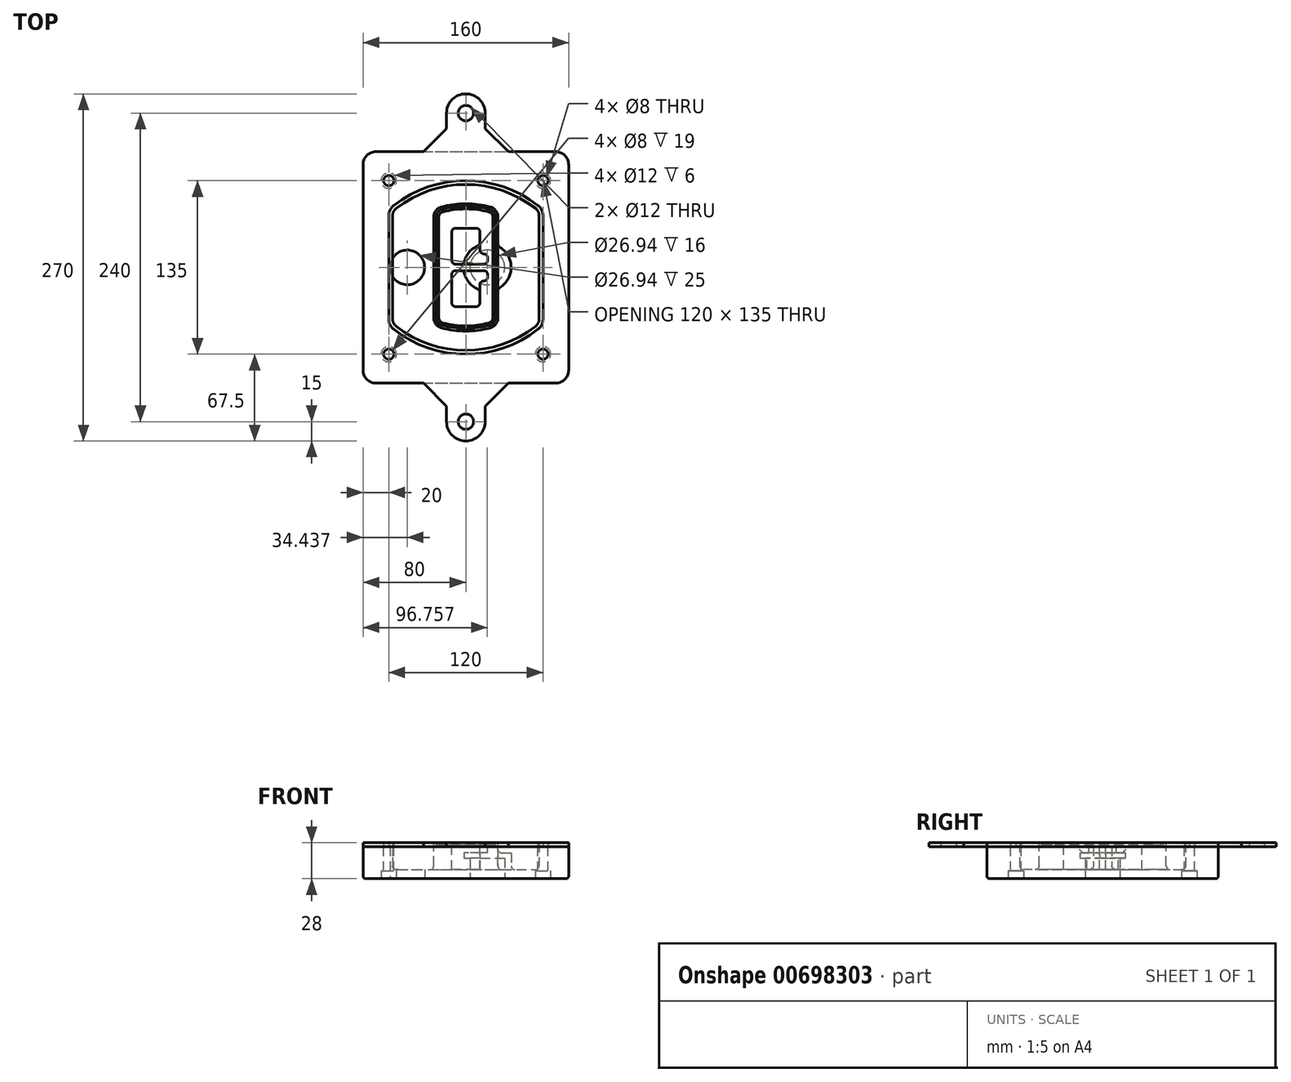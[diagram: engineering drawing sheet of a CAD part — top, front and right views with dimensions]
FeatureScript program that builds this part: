
annotation { "Feature Type Name" : "Feature", "Feature Type Description" : "" }
export const myFeature = defineFeature(function(context is Context, id is Id, definition is map)
    precondition{}
    {
        {
            var Q0;
            Q0=qCreatedBy(makeId("Top.planeOp"),FACE);
            var sketch = newSketch(context, id + "F0", { "sketchPlane" : qUnion([Q0])});
            skPoint(sketch, "E0.rect.middle", {"position": v(0, 0) * mm});
            skLineSegment(sketch, "E1.bottom", {"start": v(-70, -90) * mm, "end": v(70, -90) * mm});
            skLineSegment(sketch, "E1.top", {"start": v(-70, 90) * mm, "end": v(70, 90) * mm});
            skLineSegment(sketch, "E1.left", {"start": v(-80, -80) * mm, "end": v(-80, 80) * mm});
            skLineSegment(sketch, "E1.right", {"start": v(80, -80) * mm, "end": v(80, 80) * mm});
            skLineSegment(sketch, "E2", {"start": v(-80, 90) * mm, "end": v(80, -90) * mm, "construction": true});
            skLineSegment(sketch, "E3", {"start": v(80, 90) * mm, "end": v(-80, -90) * mm, "construction": true});
            skCircle(sketch, "E4", {"center": v(-60, 67.5) * mm, "radius": 4 * mm});
            skCircle(sketch, "E5", {"center": v(60, 67.5) * mm, "radius": 4 * mm});
            skCircle(sketch, "E6", {"center": v(60, -67.5) * mm, "radius": 4 * mm});
            skCircle(sketch, "E7", {"center": v(-60, -67.5) * mm, "radius": 4 * mm});
            skLineSegment(sketch, "E8", {"start": v(-60, 67.5) * mm, "end": v(60, 67.5) * mm, "construction": true});
            skLineSegment(sketch, "E9", {"start": v(60, 67.5) * mm, "end": v(60, -67.5) * mm, "construction": true});
            skLineSegment(sketch, "E10", {"start": v(60, -67.5) * mm, "end": v(-60, -67.5) * mm, "construction": true});
            skLineSegment(sketch, "E11", {"start": v(-60, -67.5) * mm, "end": v(-60, 67.5) * mm, "construction": true});
            skLineSegment(sketch, "E12", {"start": v(-60, 40.3) * mm, "end": v(-60, -40.3) * mm});
            skLineSegment(sketch, "E13", {"start": v(60, 40.3) * mm, "end": v(60, -40.3) * mm});
            skArc(sketch, "E14", {"start": v(56.15, 48.18) * mm, "mid": v(0, 67.5) * mm, "end": v(-56.15, 48.18) * mm});
            skArc(sketch, "E15", {"start": v(-56.15, -48.18) * mm, "mid": v(0, -67.5) * mm, "end": v(56.15, -48.18) * mm});
            skLineSegment(sketch, "E16", {"start": v(-60, 0) * mm, "end": v(60, 0) * mm, "construction": true});
            skPoint(sketch, "E17.visualSharp", {"position": v(-60, -45) * mm});
            skArc(sketch, "E17.filletArc", {"start": v(-60, -40.3) * mm, "mid": v(-58.99, -44.68) * mm, "end": v(-56.15, -48.18) * mm});
            skPoint(sketch, "E18.visualSharp", {"position": v(-60, 45) * mm});
            skArc(sketch, "E18.filletArc", {"start": v(-56.15, 48.18) * mm, "mid": v(-58.99, 44.68) * mm, "end": v(-60, 40.3) * mm});
            skPoint(sketch, "E19.visualSharp", {"position": v(60, 45) * mm});
            skArc(sketch, "E19.filletArc", {"start": v(60, 40.3) * mm, "mid": v(58.99, 44.68) * mm, "end": v(56.15, 48.18) * mm});
            skPoint(sketch, "E20.visualSharp", {"position": v(60, -45) * mm});
            skArc(sketch, "E20.filletArc", {"start": v(56.15, -48.18) * mm, "mid": v(58.99, -44.68) * mm, "end": v(60, -40.3) * mm});
            skPoint(sketch, "E21.visualSharp", {"position": v(-80, 90) * mm});
            skArc(sketch, "E21.filletArc", {"start": v(-70, 90) * mm, "mid": v(-77.07, 87.07) * mm, "end": v(-80, 80) * mm});
            skPoint(sketch, "E22.visualSharp", {"position": v(80, 90) * mm});
            skArc(sketch, "E22.filletArc", {"start": v(80, 80) * mm, "mid": v(77.07, 87.07) * mm, "end": v(70, 90) * mm});
            skPoint(sketch, "E23.visualSharp", {"position": v(80, -90) * mm});
            skArc(sketch, "E23.filletArc", {"start": v(70, -90) * mm, "mid": v(77.07, -87.07) * mm, "end": v(80, -80) * mm});
            skPoint(sketch, "E24.visualSharp", {"position": v(-80, -90) * mm});
            skArc(sketch, "E24.filletArc", {"start": v(-80, -80) * mm, "mid": v(-77.07, -87.07) * mm, "end": v(-70, -90) * mm});
            skArc(sketch, "E25.0", {"start": v(57, 40.3) * mm, "mid": v(56.3, 43.36) * mm, "end": v(54.3, 45.81) * mm});
            skLineSegment(sketch, "E25.1", {"start": v(57, 40.3) * mm, "end": v(57, -40.3) * mm});
            skArc(sketch, "E25.2", {"start": v(54.3, -45.81) * mm, "mid": v(56.3, -43.36) * mm, "end": v(57, -40.3) * mm});
            skArc(sketch, "E25.3", {"start": v(-54.3, -45.81) * mm, "mid": v(0, -64.5) * mm, "end": v(54.3, -45.81) * mm});
            skArc(sketch, "E25.4", {"start": v(-57, -40.3) * mm, "mid": v(-56.3, -43.36) * mm, "end": v(-54.3, -45.81) * mm});
            skArc(sketch, "E25.5", {"start": v(54.3, 45.81) * mm, "mid": v(0, 64.5) * mm, "end": v(-54.3, 45.81) * mm});
            skLineSegment(sketch, "E25.6", {"start": v(-57, 40.3) * mm, "end": v(-57, -40.3) * mm});
            skArc(sketch, "E25.7", {"start": v(-54.3, 45.81) * mm, "mid": v(-56.3, 43.36) * mm, "end": v(-57, 40.3) * mm});
            skArc(sketch, "E26.0", {"start": v(-58.62, 51.33) * mm, "mid": v(-62.58, 46.43) * mm, "end": v(-64, 40.3) * mm});
            skArc(sketch, "E26.1", {"start": v(58.62, 51.33) * mm, "mid": v(0, 71.5) * mm, "end": v(-58.62, 51.33) * mm});
            skArc(sketch, "E26.2", {"start": v(64, 40.3) * mm, "mid": v(62.58, 46.43) * mm, "end": v(58.62, 51.33) * mm});
            skLineSegment(sketch, "E26.3", {"start": v(64, 40.3) * mm, "end": v(64, -40.3) * mm});
            skArc(sketch, "E26.4", {"start": v(58.62, -51.33) * mm, "mid": v(62.58, -46.43) * mm, "end": v(64, -40.3) * mm});
            skLineSegment(sketch, "E26.5", {"start": v(-64, 40.3) * mm, "end": v(-64, -40.3) * mm});
            skArc(sketch, "E26.6", {"start": v(-58.62, -51.33) * mm, "mid": v(0, -71.5) * mm, "end": v(58.62, -51.33) * mm});
            skArc(sketch, "E26.7", {"start": v(-64, -40.3) * mm, "mid": v(-62.58, -46.43) * mm, "end": v(-58.62, -51.33) * mm});
            skSolve(sketch);
        }
        {
            var Q0;
            Q0=makeQuery(id+"F0.imprint","IMPRINT",FACE,{"disambiguationData":[TD([[makeQuery(id+"F0.imprint","IMPRINT",EDGE,{"derivedFrom":sQuery(id+"F0.wireOp",EDGE,"E1.bottom")}),1.0]])]});
            var Q1;
            Q1=makeQuery(id+"F0.imprint","IMPRINT",FACE,{"disambiguationData":[TD([[makeQuery(id+"F0.imprint","IMPRINT",EDGE,{"derivedFrom":sQuery(id+"F0.wireOp",EDGE,"E12")}),1.0]])]});
            var Q2;
            Q2=makeQuery(id+"F0.imprint","IMPRINT",FACE,{"disambiguationData":[TD([[makeQuery(id+"F0.imprint","IMPRINT",EDGE,{"derivedFrom":sQuery(id+"F0.wireOp",EDGE,"E25.0")}),1.0]])]});
            var Q3;
            Q3=makeQuery(id+"F0.imprint","IMPRINT",FACE,{"disambiguationData":[TD([[makeQuery(id+"F0.imprint","IMPRINT",EDGE,{"derivedFrom":sQuery(id+"F0.wireOp",EDGE,"E12")}),-1.0]])]});
            extrude(context, id + "F1", {"entities" : qUnion([Q0, Q1, Q2, Q3]), "oppositeDirection" : true, "depth" : 25 * mm, "offsetDistance" : 25 * mm});
        }
        {
            var Q0;
            Q0=makeQuery(id+"F0.imprint","IMPRINT",FACE,{"disambiguationData":[TD([[makeQuery(id+"F0.imprint","IMPRINT",EDGE,{"derivedFrom":sQuery(id+"F0.wireOp",EDGE,"E12")}),1.0]])]});
            extrude(context, id + "F2", {"entities" : qUnion([Q0]), "operationType" : NewBodyOperationType.ADD, "depth" : 3 * mm, "offsetDistance" : 25 * mm});
        }
        {
            var Q0;
            Q0=makeQuery(id+"F0.imprint","IMPRINT",FACE,{"disambiguationData":[TD([[makeQuery(id+"F0.imprint","IMPRINT",EDGE,{"derivedFrom":sQuery(id+"F0.wireOp",EDGE,"E25.0")}),1.0]])]});
            extrude(context, id + "F3", {"entities" : qUnion([Q0]), "operationType" : NewBodyOperationType.REMOVE, "oppositeDirection" : true, "depth" : 18 * mm});
        }
        {
            var Q0;
            Q0=makeQuery(id+"F2.opExtrude","CAP_FACE",FACE,{"disambiguationData":[OSD([sQuery(id+"F0.wireOp",EDGE,"E12"),sQuery(id+"F0.wireOp",EDGE,"E13"),sQuery(id+"F0.wireOp",EDGE,"E14"),sQuery(id+"F0.wireOp",EDGE,"E15"),sQuery(id+"F0.wireOp",EDGE,"E17.filletArc"),sQuery(id+"F0.wireOp",EDGE,"E18.filletArc"),sQuery(id+"F0.wireOp",EDGE,"E19.filletArc"),sQuery(id+"F0.wireOp",EDGE,"E20.filletArc"),sQuery(id+"F0.wireOp",EDGE,"E25.0"),sQuery(id+"F0.wireOp",EDGE,"E25.1"),sQuery(id+"F0.wireOp",EDGE,"E25.2"),sQuery(id+"F0.wireOp",EDGE,"E25.3"),sQuery(id+"F0.wireOp",EDGE,"E25.4"),sQuery(id+"F0.wireOp",EDGE,"E25.5"),sQuery(id+"F0.wireOp",EDGE,"E25.6"),sQuery(id+"F0.wireOp",EDGE,"E25.7")])],"isStart":false});
            var sketch = newSketch(context, id + "F4", { "sketchPlane" : qUnion([Q0])});
            skArc(sketch, "E27.0", {"start": v(-19.08, -46.97) * mm, "mid": v(0, -49.5) * mm, "end": v(19.08, -46.97) * mm});
            skArc(sketch, "E28.0", {"start": v(19.08, 46.97) * mm, "mid": v(0, 49.5) * mm, "end": v(-19.08, 46.97) * mm});
            skLineSegment(sketch, "E29", {"start": v(-25, 39.25) * mm, "end": v(-25, -39.25) * mm});
            skLineSegment(sketch, "E30", {"start": v(25, 39.25) * mm, "end": v(25, -39.25) * mm});
            skLineSegment(sketch, "E31", {"start": v(-25, 45.1) * mm, "end": v(25, 45.1) * mm, "construction": true});
            skLineSegment(sketch, "E32", {"start": v(-25, -45.1) * mm, "end": v(25, -45.1) * mm, "construction": true});
            skPoint(sketch, "E33.visualSharp", {"position": v(-25, 45.1) * mm});
            skArc(sketch, "E33.filletArc", {"start": v(-19.08, 46.97) * mm, "mid": v(-23.35, 44.11) * mm, "end": v(-25, 39.25) * mm});
            skPoint(sketch, "E34.visualSharp", {"position": v(25, 45.1) * mm});
            skArc(sketch, "E34.filletArc", {"start": v(25, 39.25) * mm, "mid": v(23.35, 44.11) * mm, "end": v(19.08, 46.97) * mm});
            skPoint(sketch, "E35.visualSharp", {"position": v(25, -45.1) * mm});
            skArc(sketch, "E35.filletArc", {"start": v(19.08, -46.97) * mm, "mid": v(23.35, -44.11) * mm, "end": v(25, -39.25) * mm});
            skPoint(sketch, "E36.visualSharp", {"position": v(-25, -45.1) * mm});
            skArc(sketch, "E36.filletArc", {"start": v(-25, -39.25) * mm, "mid": v(-23.35, -44.11) * mm, "end": v(-19.08, -46.97) * mm});
            skArc(sketch, "E37.0", {"start": v(54.3, 45.81) * mm, "mid": v(0, 64.5) * mm, "end": v(-54.3, 45.81) * mm});
            skArc(sketch, "E37.1", {"start": v(-54.3, 45.81) * mm, "mid": v(-56.3, 43.36) * mm, "end": v(-57, 40.3) * mm});
            skLineSegment(sketch, "E37.2", {"start": v(-57, 40.3) * mm, "end": v(-57, -40.3) * mm});
            skArc(sketch, "E37.3", {"start": v(-57, -40.3) * mm, "mid": v(-56.3, -43.36) * mm, "end": v(-54.3, -45.81) * mm});
            skArc(sketch, "E37.4", {"start": v(-54.3, -45.81) * mm, "mid": v(0, -64.5) * mm, "end": v(54.3, -45.81) * mm});
            skArc(sketch, "E37.5", {"start": v(54.3, -45.81) * mm, "mid": v(56.3, -43.36) * mm, "end": v(57, -40.3) * mm});
            skLineSegment(sketch, "E37.6", {"start": v(57, 40.3) * mm, "end": v(57, -40.3) * mm});
            skArc(sketch, "E37.7", {"start": v(57, 40.3) * mm, "mid": v(56.3, 43.36) * mm, "end": v(54.3, 45.81) * mm});
            skLineSegment(sketch, "E38.0", {"start": v(23, 39.25) * mm, "end": v(23, -39.25) * mm});
            skArc(sketch, "E38.1", {"start": v(18.56, -45.04) * mm, "mid": v(21.76, -42.9) * mm, "end": v(23, -39.25) * mm});
            skArc(sketch, "E38.2", {"start": v(-18.56, -45.04) * mm, "mid": v(0, -47.5) * mm, "end": v(18.56, -45.04) * mm});
            skArc(sketch, "E38.3", {"start": v(-23, -39.25) * mm, "mid": v(-21.76, -42.9) * mm, "end": v(-18.56, -45.04) * mm});
            skLineSegment(sketch, "E38.4", {"start": v(-23, 39.25) * mm, "end": v(-23, -39.25) * mm});
            skArc(sketch, "E38.5", {"start": v(23, 39.25) * mm, "mid": v(21.76, 42.9) * mm, "end": v(18.56, 45.04) * mm});
            skArc(sketch, "E38.6", {"start": v(-18.56, 45.04) * mm, "mid": v(-21.76, 42.9) * mm, "end": v(-23, 39.25) * mm});
            skArc(sketch, "E38.7", {"start": v(18.56, 45.04) * mm, "mid": v(0, 47.5) * mm, "end": v(-18.56, 45.04) * mm});
            skArc(sketch, "E39.0", {"start": v(21, 39.25) * mm, "mid": v(20.18, 41.68) * mm, "end": v(18.04, 43.1) * mm});
            skLineSegment(sketch, "E39.1", {"start": v(21, 39.25) * mm, "end": v(21, -39.25) * mm});
            skArc(sketch, "E39.2", {"start": v(18.04, -43.1) * mm, "mid": v(20.18, -41.68) * mm, "end": v(21, -39.25) * mm});
            skArc(sketch, "E39.3", {"start": v(-18.04, -43.1) * mm, "mid": v(0, -45.5) * mm, "end": v(18.04, -43.1) * mm});
            skArc(sketch, "E39.4", {"start": v(-21, -39.25) * mm, "mid": v(-20.18, -41.68) * mm, "end": v(-18.04, -43.1) * mm});
            skArc(sketch, "E39.5", {"start": v(18.04, 43.1) * mm, "mid": v(0, 45.5) * mm, "end": v(-18.04, 43.1) * mm});
            skLineSegment(sketch, "E39.6", {"start": v(-21, 39.25) * mm, "end": v(-21, -39.25) * mm});
            skArc(sketch, "E39.7", {"start": v(-18.04, 43.1) * mm, "mid": v(-20.18, 41.68) * mm, "end": v(-21, 39.25) * mm});
            skLineSegment(sketch, "E40", {"start": v(-25, 0) * mm, "end": v(25, 0) * mm, "construction": true});
            skLineSegment(sketch, "E41", {"start": v(-11, 5.5) * mm, "end": v(-11, 27.5) * mm});
            skLineSegment(sketch, "E42", {"start": v(-8, 30.5) * mm, "end": v(8, 30.5) * mm});
            skLineSegment(sketch, "E43", {"start": v(11, 27.5) * mm, "end": v(11, 13.5) * mm});
            skLineSegment(sketch, "E44", {"start": v(14, 10.5) * mm, "end": v(14, 10.5) * mm});
            skLineSegment(sketch, "E45", {"start": v(17, 7.5) * mm, "end": v(17, 5.5) * mm});
            skLineSegment(sketch, "E46", {"start": v(14, 2.5) * mm, "end": v(-8, 2.5) * mm});
            skPoint(sketch, "E47.visualSharp", {"position": v(-11, 30.5) * mm});
            skArc(sketch, "E47.filletArc", {"start": v(-8, 30.5) * mm, "mid": v(-10.12, 29.62) * mm, "end": v(-11, 27.5) * mm});
            skPoint(sketch, "E48.visualSharp", {"position": v(11, 30.5) * mm});
            skArc(sketch, "E48.filletArc", {"start": v(11, 27.5) * mm, "mid": v(10.12, 29.62) * mm, "end": v(8, 30.5) * mm});
            skPoint(sketch, "E49.visualSharp", {"position": v(11, 10.5) * mm});
            skArc(sketch, "E49.filletArc", {"start": v(11, 13.5) * mm, "mid": v(11.88, 11.38) * mm, "end": v(14, 10.5) * mm});
            skPoint(sketch, "E50.visualSharp", {"position": v(17, 10.5) * mm});
            skArc(sketch, "E50.filletArc", {"start": v(17, 7.5) * mm, "mid": v(16.12, 9.62) * mm, "end": v(14, 10.5) * mm});
            skPoint(sketch, "E51.visualSharp", {"position": v(17, 2.5) * mm});
            skArc(sketch, "E51.filletArc", {"start": v(14, 2.5) * mm, "mid": v(16.12, 3.38) * mm, "end": v(17, 5.5) * mm});
            skPoint(sketch, "E52.visualSharp", {"position": v(-11, 2.5) * mm});
            skArc(sketch, "E52.filletArc", {"start": v(-11, 5.5) * mm, "mid": v(-10.12, 3.38) * mm, "end": v(-8, 2.5) * mm});
            skLineSegment(sketch, "E53.0.MirrorCS", {"start": v(14, -2.5) * mm, "end": v(-8, -2.5) * mm});
            skArc(sketch, "E54.0.MirrorCS", {"start": v(-11, -5.5) * mm, "mid": v(-10.12, -3.38) * mm, "end": v(-8, -2.5) * mm});
            skLineSegment(sketch, "E55.0.MirrorCS", {"start": v(-11, -5.5) * mm, "end": v(-11, -27.5) * mm});
            skArc(sketch, "E56.0.MirrorCS", {"start": v(-8, -30.5) * mm, "mid": v(-10.12, -29.62) * mm, "end": v(-11, -27.5) * mm});
            skLineSegment(sketch, "E57.0.MirrorCS", {"start": v(-8, -30.5) * mm, "end": v(8, -30.5) * mm});
            skArc(sketch, "E58.0.MirrorCS", {"start": v(11, -27.5) * mm, "mid": v(10.12, -29.62) * mm, "end": v(8, -30.5) * mm});
            skLineSegment(sketch, "E59.0.MirrorCS", {"start": v(11, -27.5) * mm, "end": v(11, -13.5) * mm});
            skArc(sketch, "E60.0.MirrorCS", {"start": v(11, -13.5) * mm, "mid": v(11.88, -11.38) * mm, "end": v(14, -10.5) * mm});
            skArc(sketch, "E61.0.MirrorCS", {"start": v(17, -7.5) * mm, "mid": v(16.12, -9.62) * mm, "end": v(14, -10.5) * mm});
            skLineSegment(sketch, "E62.0.MirrorCS", {"start": v(17, -7.5) * mm, "end": v(17, -5.5) * mm});
            skArc(sketch, "E63.0.MirrorCS", {"start": v(14, -2.5) * mm, "mid": v(16.12, -3.38) * mm, "end": v(17, -5.5) * mm});
            skSolve(sketch);
        }
        {
            var Q0;
            Q0=makeQuery(id+"F4.imprint","IMPRINT",FACE,{"disambiguationData":[TD([[makeQuery(id+"F4.imprint","IMPRINT",EDGE,{"derivedFrom":sQuery(id+"F4.wireOp",EDGE,"E27.0")}),1.0]])]});
            var Q1;
            Q1=makeQuery(id+"F4.imprint","IMPRINT",FACE,{"disambiguationData":[TD([[makeQuery(id+"F4.imprint","IMPRINT",EDGE,{"derivedFrom":sQuery(id+"F4.wireOp",EDGE,"E38.0")}),-1.0]])]});
            var Q2;
            Q2=makeQuery(id+"F4.imprint","IMPRINT",FACE,{"disambiguationData":[TD([[makeQuery(id+"F4.imprint","IMPRINT",EDGE,{"derivedFrom":sQuery(id+"F4.wireOp",EDGE,"E39.0")}),1.0]])]});
            extrude(context, id + "F5", {"entities" : qUnion([Q0, Q1, Q2]), "operationType" : NewBodyOperationType.ADD, "endBound" : BoundingType.UP_TO_NEXT, "oppositeDirection" : true, "depth" : 25 * mm});
        }
        {
            var Q0;
            Q0=makeQuery(id+"F4.imprint","IMPRINT",FACE,{"disambiguationData":[TD([[makeQuery(id+"F4.imprint","IMPRINT",EDGE,{"derivedFrom":sQuery(id+"F4.wireOp",EDGE,"E38.0")}),-1.0]])]});
            extrude(context, id + "F6", {"entities" : qUnion([Q0]), "operationType" : NewBodyOperationType.REMOVE, "oppositeDirection" : true, "depth" : 2 * mm});
        }
        {
            var Q0;
            Q0=makeQuery(id+"F1.opExtrude","CAP_FACE",FACE,{"disambiguationData":[OSD([sQuery(id+"F0.wireOp",EDGE,"E1.bottom"),sQuery(id+"F0.wireOp",EDGE,"E1.top"),sQuery(id+"F0.wireOp",EDGE,"E1.left"),sQuery(id+"F0.wireOp",EDGE,"E1.right"),sQuery(id+"F0.wireOp",EDGE,"E4"),sQuery(id+"F0.wireOp",EDGE,"E5"),sQuery(id+"F0.wireOp",EDGE,"E6"),sQuery(id+"F0.wireOp",EDGE,"E7"),sQuery(id+"F0.wireOp",EDGE,"E21.filletArc"),sQuery(id+"F0.wireOp",EDGE,"E22.filletArc"),sQuery(id+"F0.wireOp",EDGE,"E23.filletArc"),sQuery(id+"F0.wireOp",EDGE,"E24.filletArc")])],"isStart":false});
            var sketch = newSketch(context, id + "F7", { "sketchPlane" : qUnion([Q0])});
            skCircle(sketch, "E64", {"center": v(16.76, 0) * mm, "radius": 13.47 * mm});
            skCircle(sketch, "E65", {"center": v(-45.56, 0) * mm, "radius": 13.47 * mm});
            skLineSegment(sketch, "E66", {"start": v(80, 0) * mm, "end": v(-80, 0) * mm});
            skCircle(sketch, "E67", {"center": v(16.76, 0) * mm, "radius": 18.47 * mm});
            skCircle(sketch, "E68", {"center": v(60, -67.5) * mm, "radius": 6 * mm});
            skCircle(sketch, "E69", {"center": v(-60, -67.5) * mm, "radius": 6 * mm});
            skCircle(sketch, "E70", {"center": v(-60, 67.5) * mm, "radius": 6 * mm});
            skCircle(sketch, "E71", {"center": v(60, 67.5) * mm, "radius": 6 * mm});
            skSolve(sketch);
        }
        {
            var Q0;
            {var subQ1=sQuery(id+"F7.wireOp",EDGE,"E66");var subQ4=sQuery(id+"F7.wireOp",EDGE,"E64");var subQ6=makeQuery(id+"F7.imprint","INTERSECT",VERTEX,{"disambiguationData":[OD(0.0)],"derivedFrom":[subQ4,subQ1]});Q0=makeQuery(id+"F7.imprint","IMPRINT",FACE,{"disambiguationData":[TD([[makeQuery(id+"F7.imprint","IMPRINT",EDGE,{"disambiguationData":[TD([[subQ6,-1.0]])],"derivedFrom":subQ4}),-1.0]])]});}
            var Q1;
            {var subQ0=sQuery(id+"F7.wireOp",EDGE,"E66");var subQ1=sQuery(id+"F7.wireOp",EDGE,"E64");var subQ3=makeQuery(id+"F7.imprint","INTERSECT",VERTEX,{"disambiguationData":[OD(0.0)],"derivedFrom":[subQ1,subQ0]});Q1=makeQuery(id+"F7.imprint","IMPRINT",FACE,{"disambiguationData":[TD([[makeQuery(id+"F7.imprint","IMPRINT",EDGE,{"disambiguationData":[TD([[subQ3,-1.0]])],"derivedFrom":subQ1}),1.0]])]});}
            var Q2;
            {var subQ0=sQuery(id+"F7.wireOp",EDGE,"E66");var subQ1=sQuery(id+"F7.wireOp",EDGE,"E64");var subQ3=makeQuery(id+"F7.imprint","INTERSECT",VERTEX,{"disambiguationData":[OD(0.0)],"derivedFrom":[subQ1,subQ0]});Q2=makeQuery(id+"F7.imprint","IMPRINT",FACE,{"disambiguationData":[TD([[makeQuery(id+"F7.imprint","IMPRINT",EDGE,{"disambiguationData":[TD([[subQ3,1.0]])],"derivedFrom":subQ1}),1.0]])]});}
            var Q3;
            {var subQ1=sQuery(id+"F7.wireOp",EDGE,"E66");var subQ4=sQuery(id+"F7.wireOp",EDGE,"E64");var subQ6=makeQuery(id+"F7.imprint","INTERSECT",VERTEX,{"disambiguationData":[OD(0.0)],"derivedFrom":[subQ4,subQ1]});Q3=makeQuery(id+"F7.imprint","IMPRINT",FACE,{"disambiguationData":[TD([[makeQuery(id+"F7.imprint","IMPRINT",EDGE,{"disambiguationData":[TD([[subQ6,1.0]])],"derivedFrom":subQ4}),-1.0]])]});}
            extrude(context, id + "F8", {"entities" : qUnion([Q0, Q1, Q2, Q3]), "operationType" : NewBodyOperationType.ADD, "oppositeDirection" : true, "depth" : 20 * mm});
        }
        {
            var Q0;
            {var subQ0=sQuery(id+"F7.wireOp",EDGE,"E66");var subQ1=sQuery(id+"F7.wireOp",EDGE,"E64");var subQ3=makeQuery(id+"F7.imprint","INTERSECT",VERTEX,{"disambiguationData":[OD(0.0)],"derivedFrom":[subQ1,subQ0]});Q0=makeQuery(id+"F7.imprint","IMPRINT",FACE,{"disambiguationData":[TD([[makeQuery(id+"F7.imprint","IMPRINT",EDGE,{"disambiguationData":[TD([[subQ3,-1.0]])],"derivedFrom":subQ1}),1.0]])]});}
            var Q1;
            {var subQ0=sQuery(id+"F7.wireOp",EDGE,"E66");var subQ1=sQuery(id+"F7.wireOp",EDGE,"E64");var subQ3=makeQuery(id+"F7.imprint","INTERSECT",VERTEX,{"disambiguationData":[OD(0.0)],"derivedFrom":[subQ1,subQ0]});Q1=makeQuery(id+"F7.imprint","IMPRINT",FACE,{"disambiguationData":[TD([[makeQuery(id+"F7.imprint","IMPRINT",EDGE,{"disambiguationData":[TD([[subQ3,1.0]])],"derivedFrom":subQ1}),1.0]])]});}
            extrude(context, id + "F9", {"entities" : qUnion([Q0, Q1]), "operationType" : NewBodyOperationType.REMOVE, "oppositeDirection" : true, "depth" : 16 * mm});
        }
        {
            var Q0;
            {var subQ0=sQuery(id+"F7.wireOp",EDGE,"E66");var subQ1=sQuery(id+"F7.wireOp",EDGE,"E65");var subQ3=makeQuery(id+"F7.imprint","INTERSECT",VERTEX,{"disambiguationData":[OD(0.0)],"derivedFrom":[subQ1,subQ0]});Q0=makeQuery(id+"F7.imprint","IMPRINT",FACE,{"disambiguationData":[TD([[makeQuery(id+"F7.imprint","IMPRINT",EDGE,{"disambiguationData":[TD([[subQ3,-1.0]])],"derivedFrom":subQ1}),1.0]])]});}
            var Q1;
            {var subQ0=sQuery(id+"F7.wireOp",EDGE,"E66");var subQ1=sQuery(id+"F7.wireOp",EDGE,"E65");var subQ3=makeQuery(id+"F7.imprint","INTERSECT",VERTEX,{"disambiguationData":[OD(0.0)],"derivedFrom":[subQ1,subQ0]});Q1=makeQuery(id+"F7.imprint","IMPRINT",FACE,{"disambiguationData":[TD([[makeQuery(id+"F7.imprint","IMPRINT",EDGE,{"disambiguationData":[TD([[subQ3,1.0]])],"derivedFrom":subQ1}),1.0]])]});}
            extrude(context, id + "F10", {"entities" : qUnion([Q0, Q1]), "operationType" : NewBodyOperationType.REMOVE, "oppositeDirection" : true, "depth" : 25 * mm});
        }
        {
            var Q0;
            Q0=makeQuery(id+"F7.imprint","IMPRINT",FACE,{"disambiguationData":[TD([[makeQuery(id+"F7.imprint","IMPRINT",EDGE,{"derivedFrom":sQuery(id+"F7.wireOp",EDGE,"E68")}),1.0]])]});
            var Q1;
            Q1=makeQuery(id+"F7.imprint","IMPRINT",FACE,{"disambiguationData":[TD([[makeQuery(id+"F7.imprint","IMPRINT",EDGE,{"derivedFrom":makeQuery(id+"F1.opExtrude","CAP_EDGE",EDGE,{"disambiguationData":[OSD([sQuery(id+"F0.wireOp",EDGE,"E5")])],"isStart":false})}),-1.0]])]});
            var Q2;
            Q2=makeQuery(id+"F7.imprint","IMPRINT",FACE,{"disambiguationData":[TD([[makeQuery(id+"F7.imprint","IMPRINT",EDGE,{"derivedFrom":sQuery(id+"F7.wireOp",EDGE,"E69")}),1.0]])]});
            var Q3;
            Q3=makeQuery(id+"F7.imprint","IMPRINT",FACE,{"disambiguationData":[TD([[makeQuery(id+"F7.imprint","IMPRINT",EDGE,{"derivedFrom":makeQuery(id+"F1.opExtrude","CAP_EDGE",EDGE,{"disambiguationData":[OSD([sQuery(id+"F0.wireOp",EDGE,"E4")])],"isStart":false})}),-1.0]])]});
            var Q4;
            Q4=makeQuery(id+"F7.imprint","IMPRINT",FACE,{"disambiguationData":[TD([[makeQuery(id+"F7.imprint","IMPRINT",EDGE,{"derivedFrom":sQuery(id+"F7.wireOp",EDGE,"E70")}),1.0]])]});
            var Q5;
            Q5=makeQuery(id+"F7.imprint","IMPRINT",FACE,{"disambiguationData":[TD([[makeQuery(id+"F7.imprint","IMPRINT",EDGE,{"derivedFrom":makeQuery(id+"F1.opExtrude","CAP_EDGE",EDGE,{"disambiguationData":[OSD([sQuery(id+"F0.wireOp",EDGE,"E7")])],"isStart":false})}),-1.0]])]});
            var Q6;
            Q6=makeQuery(id+"F7.imprint","IMPRINT",FACE,{"disambiguationData":[TD([[makeQuery(id+"F7.imprint","IMPRINT",EDGE,{"derivedFrom":sQuery(id+"F7.wireOp",EDGE,"E71")}),1.0]])]});
            var Q7;
            Q7=makeQuery(id+"F7.imprint","IMPRINT",FACE,{"disambiguationData":[TD([[makeQuery(id+"F7.imprint","IMPRINT",EDGE,{"derivedFrom":makeQuery(id+"F1.opExtrude","CAP_EDGE",EDGE,{"disambiguationData":[OSD([sQuery(id+"F0.wireOp",EDGE,"E6")])],"isStart":false})}),-1.0]])]});
            extrude(context, id + "F11", {"entities" : qUnion([Q0, Q1, Q2, Q3, Q4, Q5, Q6, Q7]), "operationType" : NewBodyOperationType.REMOVE, "oppositeDirection" : true, "depth" : 6 * mm});
        }
        {
            var Q0;
            Q0=makeQuery(id+"F9.boolean.opBoolean","COPY",FACE,{"derivedFrom":makeQuery(id+"F9.opExtrude","CAP_FACE",FACE,{"disambiguationData":[OSD([sQuery(id+"F7.wireOp",EDGE,"E64")])],"isStart":false})});
            var sketch = newSketch(context, id + "F12", { "sketchPlane" : qUnion([Q0])});
            skArc(sketch, "E72.0", {"start": v(11, 17.55) * mm, "mid": v(2.57, 11.82) * mm, "end": v(-1.54, 2.5) * mm});
            skArc(sketch, "E72.1", {"start": v(-1.54, -2.5) * mm, "mid": v(2.57, -11.82) * mm, "end": v(11, -17.55) * mm});
            skLineSegment(sketch, "E73", {"start": v(-1.54, -2.5) * mm, "end": v(14, -2.5) * mm});
            skLineSegment(sketch, "E74.0", {"start": v(14, 2.5) * mm, "end": v(-1.54, 2.5) * mm});
            skArc(sketch, "E74.1", {"start": v(14, 2.5) * mm, "mid": v(16.12, 3.38) * mm, "end": v(17, 5.5) * mm});
            skLineSegment(sketch, "E74.2", {"start": v(17, 7.5) * mm, "end": v(17, 5.5) * mm});
            skArc(sketch, "E74.3", {"start": v(17, 7.5) * mm, "mid": v(16.12, 9.62) * mm, "end": v(14, 10.5) * mm});
            skArc(sketch, "E74.4", {"start": v(11, 13.5) * mm, "mid": v(11.88, 11.38) * mm, "end": v(14, 10.5) * mm});
            skLineSegment(sketch, "E74.5", {"start": v(11, 17.55) * mm, "end": v(11, 13.5) * mm});
            skLineSegment(sketch, "E74.7", {"start": v(14, -2.5) * mm, "end": v(-1.54, -2.5) * mm});
            skArc(sketch, "E74.8", {"start": v(14, -2.5) * mm, "mid": v(16.12, -3.38) * mm, "end": v(17, -5.5) * mm});
            skLineSegment(sketch, "E74.9", {"start": v(17, -7.5) * mm, "end": v(17, -5.5) * mm});
            skArc(sketch, "E74.10", {"start": v(17, -7.5) * mm, "mid": v(16.12, -9.62) * mm, "end": v(14, -10.5) * mm});
            skArc(sketch, "E74.11", {"start": v(11, -13.5) * mm, "mid": v(11.88, -11.38) * mm, "end": v(14, -10.5) * mm});
            skLineSegment(sketch, "E74.12", {"start": v(11, -17.55) * mm, "end": v(11, -13.5) * mm});
            skPoint(sketch, "E75.orphan", {"position": v(11, -27.5) * mm});
            skPoint(sketch, "E76.orphan", {"position": v(-8, -2.5) * mm});
            skPoint(sketch, "E77.orphan", {"position": v(-8, 2.5) * mm});
            skPoint(sketch, "E78.orphan", {"position": v(11, 27.5) * mm});
            skSolve(sketch);
        }
        {
            var Q0;
            {var subQ7=sQuery(id+"F12.wireOp",EDGE,"E72.0");var subQ14=sQuery(id+"F12.wireOp",EDGE,"E72.1");var subQ16=sQuery(id+"F12.wireOp",EDGE,"E74.1");var subQ18=sQuery(id+"F12.wireOp",EDGE,"E74.8");Q0=qUnion([makeQuery(id+"F12.imprint","IMPRINT",FACE,{"disambiguationData":[TD([[makeQuery(id+"F12.imprint","IMPRINT",EDGE,{"derivedFrom":subQ7}),1.0]])]}),makeQuery(id+"F12.imprint","IMPRINT",FACE,{"disambiguationData":[TD([[makeQuery(id+"F12.imprint","IMPRINT",EDGE,{"derivedFrom":subQ14}),1.0]])]}),makeQuery(id+"F12.imprint","IMPRINT",FACE,{"disambiguationData":[TD([[makeQuery(id+"F12.imprint","IMPRINT",EDGE,{"derivedFrom":subQ16}),1.0]])]}),makeQuery(id+"F12.imprint","IMPRINT",FACE,{"disambiguationData":[TD([[makeQuery(id+"F12.imprint","IMPRINT",EDGE,{"derivedFrom":subQ18}),-1.0]])]})]);}
            var Q1;
            Q1=makeQuery(id+"F5.boolean.opBoolean","SPLIT",FACE,{"disambiguationData":[TD([makeQuery(id+"F5.opExtrude","SWEPT_FACE",FACE,{"disambiguationData":[OSD([sQuery(id+"F4.wireOp",EDGE,"E41")])]})])],"derivedFrom":makeQuery(id+"F3.boolean.opBoolean","COPY",FACE,{"derivedFrom":makeQuery(id+"F3.opExtrude","CAP_FACE",FACE,{"disambiguationData":[OSD([sQuery(id+"F0.wireOp",EDGE,"E25.0"),sQuery(id+"F0.wireOp",EDGE,"E25.1"),sQuery(id+"F0.wireOp",EDGE,"E25.2"),sQuery(id+"F0.wireOp",EDGE,"E25.3"),sQuery(id+"F0.wireOp",EDGE,"E25.4"),sQuery(id+"F0.wireOp",EDGE,"E25.5"),sQuery(id+"F0.wireOp",EDGE,"E25.6"),sQuery(id+"F0.wireOp",EDGE,"E25.7")])],"isStart":false})})});
            extrude(context, id + "F13", {"entities" : qUnion([Q0]), "operationType" : NewBodyOperationType.REMOVE, "endBound" : BoundingType.UP_TO_SURFACE, "endBoundEntityFace" : qUnion([Q1]), "depth" : 25 * mm});
        }
        {
            var Q0;
            Q0=makeQuery(id+"F3.boolean.opBoolean","COPY",EDGE,{"derivedFrom":makeQuery(id+"F3.opExtrude","CAP_EDGE",EDGE,{"disambiguationData":[OSD([sQuery(id+"F0.wireOp",EDGE,"E25.6")])],"isStart":false})});
            var Q1;
            Q1=makeQuery(id+"F8.boolean.opBoolean","INTERSECT",EDGE,{"derivedFrom":[makeQuery(id+"F5.opExtrude","SWEPT_FACE",FACE,{"disambiguationData":[OSD([sQuery(id+"F4.wireOp",EDGE,"E30")])]}),makeQuery(id+"F8.opExtrude","CAP_FACE",FACE,{"disambiguationData":[OSD([sQuery(id+"F7.wireOp",EDGE,"E67")])],"isStart":false})]});
            var Q2;
            Q2=makeQuery(id+"F8.boolean.opBoolean","INTERSECT",EDGE,{"disambiguationData":[OD(1.0)],"derivedFrom":[makeQuery(id+"F5.opExtrude","SWEPT_FACE",FACE,{"disambiguationData":[OSD([sQuery(id+"F4.wireOp",EDGE,"E30")])]}),makeQuery(id+"F8.opExtrude","SWEPT_FACE",FACE,{"disambiguationData":[OSD([sQuery(id+"F7.wireOp",EDGE,"E67")])]})]});
            var Q3;
            {var subQ0=sQuery(id+"F4.wireOp",EDGE,"E30");Q3=makeQuery(id+"F8.boolean.opBoolean","SPLIT",EDGE,{"disambiguationData":[TD([makeQuery(id+"F5.opExtrude","SWEPT_FACE",FACE,{"disambiguationData":[OSD([sQuery(id+"F4.wireOp",EDGE,"E35.filletArc")])]})])],"derivedFrom":makeQuery(id+"F5.opExtrude","CAP_EDGE",EDGE,{"disambiguationData":[OSD([subQ0])],"isStart":false})});}
            var Q4;
            {var subQ0=sQuery(id+"F0.wireOp",EDGE,"E25.7");var subQ1=sQuery(id+"F0.wireOp",EDGE,"E25.1");var subQ2=sQuery(id+"F0.wireOp",EDGE,"E25.6");var subQ3=sQuery(id+"F0.wireOp",EDGE,"E25.5");var subQ4=sQuery(id+"F0.wireOp",EDGE,"E25.4");var subQ5=sQuery(id+"F0.wireOp",EDGE,"E25.0");var subQ6=sQuery(id+"F0.wireOp",EDGE,"E25.2");var subQ7=sQuery(id+"F0.wireOp",EDGE,"E25.3");Q4=makeQuery(id+"F8.boolean.opBoolean","INTERSECT",EDGE,{"derivedFrom":[makeQuery(id+"F5.boolean.opBoolean","SPLIT",FACE,{"disambiguationData":[TD([makeQuery(id+"F2.opExtrude","SWEPT_FACE",FACE,{"disambiguationData":[OSD([subQ5])]})])],"derivedFrom":makeQuery(id+"F3.boolean.opBoolean","COPY",FACE,{"derivedFrom":makeQuery(id+"F3.opExtrude","CAP_FACE",FACE,{"disambiguationData":[OSD([subQ5,subQ1,subQ6,subQ7,subQ4,subQ3,subQ2,subQ0])],"isStart":false})})}),makeQuery(id+"F8.opExtrude","SWEPT_FACE",FACE,{"disambiguationData":[OSD([sQuery(id+"F7.wireOp",EDGE,"E67")])]})]});}
            var Q5;
            Q5=makeQuery(id+"F8.boolean.opBoolean","INTERSECT",EDGE,{"disambiguationData":[OD(0.0)],"derivedFrom":[makeQuery(id+"F5.opExtrude","SWEPT_FACE",FACE,{"disambiguationData":[OSD([sQuery(id+"F4.wireOp",EDGE,"E30")])]}),makeQuery(id+"F8.opExtrude","SWEPT_FACE",FACE,{"disambiguationData":[OSD([sQuery(id+"F7.wireOp",EDGE,"E67")])]})]});
            fillet(context, id + "F14", {"entities" : qUnion([Q0, Q1, Q2, Q3, Q4, Q5]), "radius" : 3 * mm, "tangentPropagation" : true, "allowEdgeOverflow" : false});
        }
        {
            var Q0;
            Q0=makeQuery(id+"F1.opExtrude","CAP_EDGE",EDGE,{"disambiguationData":[OSD([sQuery(id+"F0.wireOp",EDGE,"E1.bottom")])],"isStart":false});
            fillet(context, id + "F15", {"entities" : qUnion([Q0]), "radius" : 2 * mm, "tangentPropagation" : true, "allowEdgeOverflow" : false});
        }
        {
            var Q0;
            {var subQ0=sQuery(id+"F0.wireOp",EDGE,"E21.filletArc");var subQ1=sQuery(id+"F0.wireOp",EDGE,"E7");var subQ2=sQuery(id+"F0.wireOp",EDGE,"E6");var subQ3=sQuery(id+"F0.wireOp",EDGE,"E5");var subQ4=sQuery(id+"F0.wireOp",EDGE,"E4");var subQ5=sQuery(id+"F0.wireOp",EDGE,"E22.filletArc");var subQ6=sQuery(id+"F0.wireOp",EDGE,"E1.bottom");var subQ7=sQuery(id+"F0.wireOp",EDGE,"E1.right");var subQ8=sQuery(id+"F0.wireOp",EDGE,"E1.top");var subQ9=sQuery(id+"F0.wireOp",EDGE,"E1.left");var subQ10=sQuery(id+"F0.wireOp",EDGE,"E23.filletArc");var subQ11=sQuery(id+"F0.wireOp",EDGE,"E24.filletArc");Q0=makeQuery(id+"F2.boolean.opBoolean","SPLIT",FACE,{"disambiguationData":[TD([makeQuery(id+"F1.opExtrude","SWEPT_FACE",FACE,{"disambiguationData":[OSD([subQ6])]})])],"derivedFrom":makeQuery(id+"F1.opExtrude","CAP_FACE",FACE,{"disambiguationData":[OSD([subQ6,subQ8,subQ9,subQ7,subQ4,subQ3,subQ2,subQ1,subQ0,subQ5,subQ10,subQ11])],"isStart":true})});}
            var sketch = newSketch(context, id + "F16", { "sketchPlane" : qUnion([Q0])});
            skPoint(sketch, "E79.endSnap0", {"position": v(0, 90) * mm});
            skLineSegment(sketch, "E80", {"start": v(33, 90) * mm, "end": v(15, 108) * mm});
            skLineSegment(sketch, "E81", {"start": v(-33, 90) * mm, "end": v(-15, 108) * mm});
            skLineSegment(sketch, "E82", {"start": v(15, 108) * mm, "end": v(15, 120) * mm});
            skLineSegment(sketch, "E83", {"start": v(-15, 108) * mm, "end": v(-15, 120) * mm});
            skArc(sketch, "E84", {"start": v(15, 120) * mm, "mid": v(0, 135) * mm, "end": v(-15, 120) * mm});
            skCircle(sketch, "E85", {"center": v(0, 120) * mm, "radius": 6 * mm});
            skLineSegment(sketch, "E86", {"start": v(-80, 0) * mm, "end": v(80, 0) * mm, "construction": true});
            skLineSegment(sketch, "E87", {"start": v(0, 120) * mm, "end": v(0, 90) * mm, "construction": true});
            skLineSegment(sketch, "E88.MirrorCS", {"start": v(33, -90) * mm, "end": v(15, -108) * mm});
            skLineSegment(sketch, "E89.MirrorCS", {"start": v(-33, -90) * mm, "end": v(-15, -108) * mm});
            skLineSegment(sketch, "E90.MirrorCS", {"start": v(-15, -108) * mm, "end": v(-15, -120) * mm});
            skArc(sketch, "E91.MirrorCS", {"start": v(15, -120) * mm, "mid": v(0, -135) * mm, "end": v(-15, -120) * mm});
            skLineSegment(sketch, "E92.MirrorCS", {"start": v(15, -108) * mm, "end": v(15, -120) * mm});
            skLineSegment(sketch, "E93.MirrorCS", {"start": v(0, -120) * mm, "end": v(0, -90) * mm, "construction": true});
            skCircle(sketch, "E94.MirrorC", {"center": v(0, -120) * mm, "radius": 6 * mm});
            skLineSegment(sketch, "E95", {"start": v(33, 90) * mm, "end": v(-33, 90) * mm, "construction": true});
            skLineSegment(sketch, "E96", {"start": v(33, -90) * mm, "end": v(-33, -90) * mm, "construction": true});
            skSolve(sketch);
        }
        {
            var Q0;
            {var subQ1=sQuery(id+"F16.wireOp",EDGE,"E88.MirrorCS");Q0=makeQuery(id+"F16.imprint","IMPRINT",FACE,{"disambiguationData":[TD([[makeQuery(id+"F16.imprint","IMPRINT",EDGE,{"derivedFrom":subQ1}),-1.0]])]});}
            var Q1;
            Q1=makeQuery(id+"F16.imprint","IMPRINT",FACE,{"disambiguationData":[TD([[makeQuery(id+"F16.imprint","IMPRINT",EDGE,{"derivedFrom":makeQuery(id+"F1.opExtrude","CAP_EDGE",EDGE,{"disambiguationData":[OSD([sQuery(id+"F0.wireOp",EDGE,"E1.left")])],"isStart":true})}),-1.0]])]});
            var Q2;
            {var subQ0=sQuery(id+"F16.wireOp",EDGE,"E80");Q2=makeQuery(id+"F16.imprint","IMPRINT",FACE,{"disambiguationData":[TD([[makeQuery(id+"F16.imprint","IMPRINT",EDGE,{"derivedFrom":subQ0}),1.0]])]});}
            var Q3;
            Q3=makeQuery(id+"F2.opExtrude","CAP_FACE",FACE,{"disambiguationData":[OSD([sQuery(id+"F0.wireOp",EDGE,"E12"),sQuery(id+"F0.wireOp",EDGE,"E13"),sQuery(id+"F0.wireOp",EDGE,"E14"),sQuery(id+"F0.wireOp",EDGE,"E15"),sQuery(id+"F0.wireOp",EDGE,"E17.filletArc"),sQuery(id+"F0.wireOp",EDGE,"E18.filletArc"),sQuery(id+"F0.wireOp",EDGE,"E19.filletArc"),sQuery(id+"F0.wireOp",EDGE,"E20.filletArc"),sQuery(id+"F0.wireOp",EDGE,"E25.0"),sQuery(id+"F0.wireOp",EDGE,"E25.1"),sQuery(id+"F0.wireOp",EDGE,"E25.2"),sQuery(id+"F0.wireOp",EDGE,"E25.3"),sQuery(id+"F0.wireOp",EDGE,"E25.4"),sQuery(id+"F0.wireOp",EDGE,"E25.5"),sQuery(id+"F0.wireOp",EDGE,"E25.6"),sQuery(id+"F0.wireOp",EDGE,"E25.7")])],"isStart":false});
            extrude(context, id + "F17", {"entities" : qUnion([Q0, Q1, Q2]), "endBound" : BoundingType.UP_TO_SURFACE, "depth" : 25 * mm, "endBoundEntityFace" : qUnion([Q3]), "offsetDistance" : 25 * mm});
        }
    });
